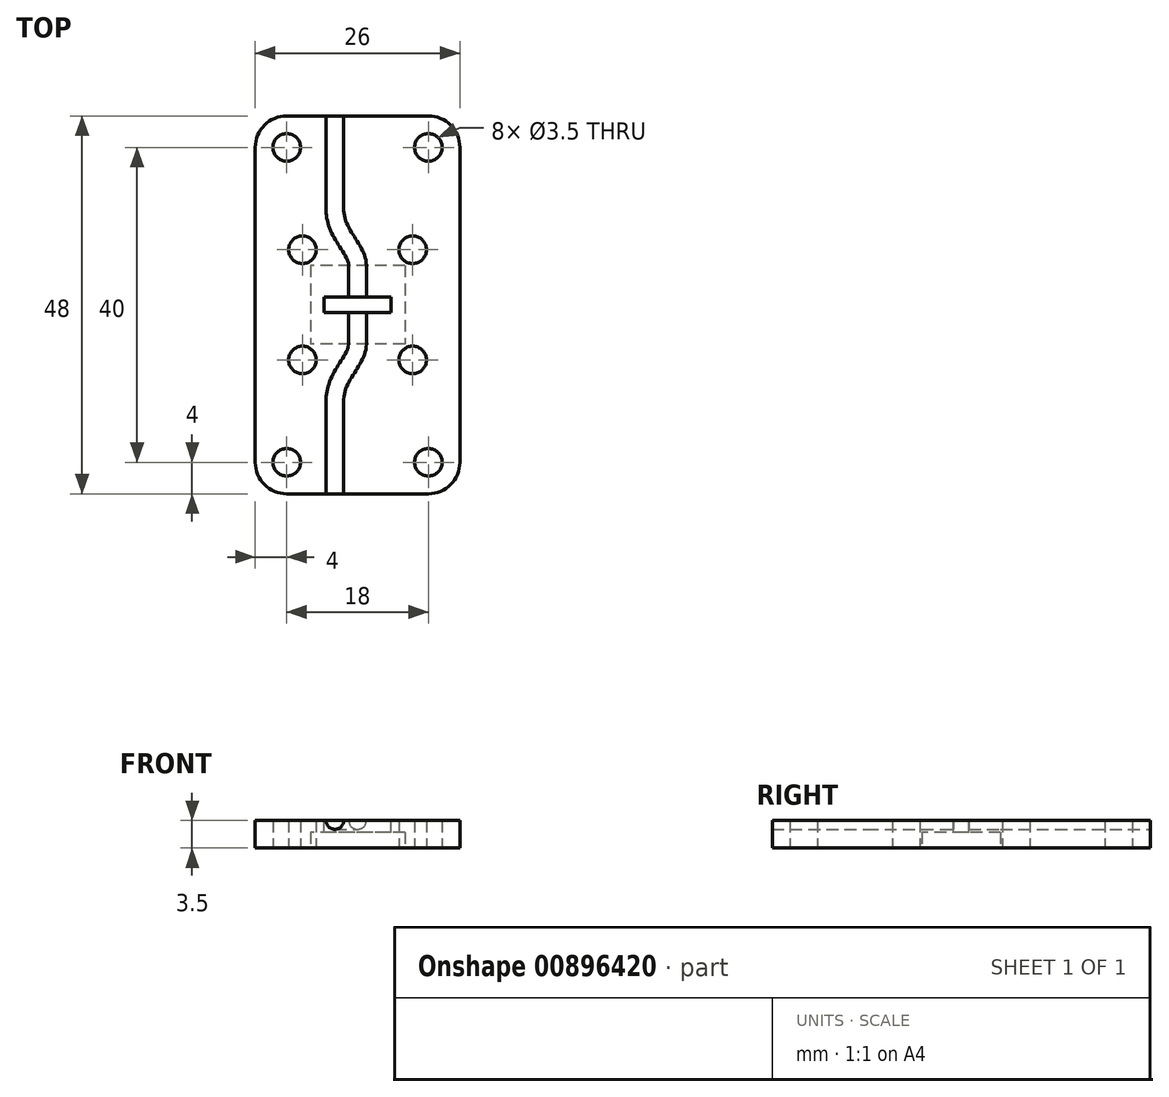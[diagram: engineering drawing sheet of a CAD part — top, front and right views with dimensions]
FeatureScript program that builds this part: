
annotation { "Feature Type Name" : "Feature", "Feature Type Description" : "" }
export const myFeature = defineFeature(function(context is Context, id is Id, definition is map)
    precondition{}
    {
        {
            var Q0;
            Q0=qCreatedBy(makeId("Top.planeOp"),FACE);
            var sketch = newSketch(context, id + "F0", { "sketchPlane" : qUnion([Q0])});
            skCircle(sketch, "E0", {"center": v(-7, 7) * mm, "radius": 1.75 * mm});
            skCircle(sketch, "E1", {"center": v(7, 7) * mm, "radius": 1.75 * mm});
            skCircle(sketch, "E2", {"center": v(7, -7) * mm, "radius": 1.75 * mm});
            skCircle(sketch, "E3", {"center": v(-7, -7) * mm, "radius": 1.75 * mm});
            skCircle(sketch, "E4", {"center": v(9, 20) * mm, "radius": 1.75 * mm});
            skCircle(sketch, "E5", {"center": v(-9, 20) * mm, "radius": 1.75 * mm});
            skCircle(sketch, "E6", {"center": v(-9, -20) * mm, "radius": 1.75 * mm});
            skCircle(sketch, "E7", {"center": v(9, -20) * mm, "radius": 1.75 * mm});
            skArc(sketch, "E8", {"start": v(-9, -24) * mm, "mid": v(-11.83, -22.83) * mm, "end": v(-13, -20) * mm});
            skArc(sketch, "E9", {"start": v(-13, 20) * mm, "mid": v(-11.83, 22.83) * mm, "end": v(-9, 24) * mm});
            skArc(sketch, "E10", {"start": v(9, 24) * mm, "mid": v(11.83, 22.83) * mm, "end": v(13, 20) * mm});
            skArc(sketch, "E11", {"start": v(13, -20) * mm, "mid": v(11.83, -22.83) * mm, "end": v(9, -24) * mm});
            skLineSegment(sketch, "E12", {"start": v(-13, -20) * mm, "end": v(-13, 20) * mm});
            skLineSegment(sketch, "E13", {"start": v(-9, 24) * mm, "end": v(9, 24) * mm});
            skLineSegment(sketch, "E14", {"start": v(13, 20) * mm, "end": v(13, -20) * mm});
            skLineSegment(sketch, "E15", {"start": v(9, -24) * mm, "end": v(-9, -24) * mm});
            skLineSegment(sketch, "E16.bottom", {"start": v(6, 5) * mm, "end": v(-6, 5) * mm});
            skLineSegment(sketch, "E16.top", {"start": v(6, -5) * mm, "end": v(-6, -5) * mm});
            skLineSegment(sketch, "E16.left", {"start": v(6, 5) * mm, "end": v(6, -5) * mm});
            skLineSegment(sketch, "E16.right", {"start": v(-6, 5) * mm, "end": v(-6, -5) * mm});
            skPoint(sketch, "E16.middle", {"position": v(0, 0) * mm});
            skSolve(sketch);
        }
        {
            var Q0;
            Q0=qSketchRegion(id+"F0",true);
            extrude(context, id + "F1", {"entities" : qUnion([Q0]), "depth" : 2 * mm, "offsetDistance" : 25 * mm});
        }
        {
            var Q0;
            Q0=makeQuery(id+"F1.opExtrude","CAP_FACE",FACE,{"disambiguationData":[OSD([sQuery(id+"F0.wireOp",EDGE,"E0"),sQuery(id+"F0.wireOp",EDGE,"E1"),sQuery(id+"F0.wireOp",EDGE,"E2"),sQuery(id+"F0.wireOp",EDGE,"E3"),sQuery(id+"F0.wireOp",EDGE,"E4"),sQuery(id+"F0.wireOp",EDGE,"E5"),sQuery(id+"F0.wireOp",EDGE,"E6"),sQuery(id+"F0.wireOp",EDGE,"E7"),sQuery(id+"F0.wireOp",EDGE,"E8"),sQuery(id+"F0.wireOp",EDGE,"E9"),sQuery(id+"F0.wireOp",EDGE,"E10"),sQuery(id+"F0.wireOp",EDGE,"E11"),sQuery(id+"F0.wireOp",EDGE,"E12"),sQuery(id+"F0.wireOp",EDGE,"E13"),sQuery(id+"F0.wireOp",EDGE,"E14"),sQuery(id+"F0.wireOp",EDGE,"E15"),sQuery(id+"F0.wireOp",EDGE,"E16.bottom"),sQuery(id+"F0.wireOp",EDGE,"E16.top"),sQuery(id+"F0.wireOp",EDGE,"E16.left"),sQuery(id+"F0.wireOp",EDGE,"E16.right")])],"isStart":false});
            var sketch = newSketch(context, id + "F2", { "sketchPlane" : qUnion([Q0])});
            skCircle(sketch, "E17", {"center": v(-7, 7) * mm, "radius": 1.75 * mm});
            skCircle(sketch, "E18", {"center": v(7, -7) * mm, "radius": 1.75 * mm});
            skCircle(sketch, "E19", {"center": v(-7, -7) * mm, "radius": 1.75 * mm});
            skCircle(sketch, "E20", {"center": v(-9, -20) * mm, "radius": 1.75 * mm});
            skCircle(sketch, "E21", {"center": v(-9, 20) * mm, "radius": 1.75 * mm});
            skCircle(sketch, "E22", {"center": v(9, 20) * mm, "radius": 1.75 * mm});
            skCircle(sketch, "E23", {"center": v(9, -20) * mm, "radius": 1.75 * mm});
            skCircle(sketch, "E24", {"center": v(7, 7) * mm, "radius": 1.75 * mm});
            skArc(sketch, "E25", {"start": v(-9, -24) * mm, "mid": v(-11.83, -22.83) * mm, "end": v(-13, -20) * mm});
            skArc(sketch, "E26", {"start": v(-13, 20) * mm, "mid": v(-11.83, 22.83) * mm, "end": v(-9, 24) * mm});
            skArc(sketch, "E27", {"start": v(9, 24) * mm, "mid": v(11.83, 22.83) * mm, "end": v(13, 20) * mm});
            skArc(sketch, "E28", {"start": v(13, -20) * mm, "mid": v(11.83, -22.83) * mm, "end": v(9, -24) * mm});
            skLineSegment(sketch, "E29", {"start": v(-13, -20) * mm, "end": v(-13, 20) * mm});
            skLineSegment(sketch, "E30", {"start": v(-9, 24) * mm, "end": v(9, 24) * mm});
            skLineSegment(sketch, "E31", {"start": v(13, 20) * mm, "end": v(13, -20) * mm});
            skLineSegment(sketch, "E32", {"start": v(9, -24) * mm, "end": v(-9, -24) * mm});
            skSolve(sketch);
        }
        {
            var Q0;
            Q0=qSketchRegion(id+"F2",true);
            extrude(context, id + "F3", {"entities" : qUnion([Q0]), "operationType" : NewBodyOperationType.ADD, "depth" : 1.5 * mm, "offsetDistance" : 25 * mm});
        }
        {
            var Q0;
            Q0=makeQuery(id+"F3.opExtrude","CAP_FACE",FACE,{"disambiguationData":[OSD([sQuery(id+"F2.wireOp",EDGE,"E17"),sQuery(id+"F2.wireOp",EDGE,"E18"),sQuery(id+"F2.wireOp",EDGE,"E19"),sQuery(id+"F2.wireOp",EDGE,"E20"),sQuery(id+"F2.wireOp",EDGE,"E21"),sQuery(id+"F2.wireOp",EDGE,"E22"),sQuery(id+"F2.wireOp",EDGE,"E23"),sQuery(id+"F2.wireOp",EDGE,"E24"),sQuery(id+"F2.wireOp",EDGE,"E25"),sQuery(id+"F2.wireOp",EDGE,"E26"),sQuery(id+"F2.wireOp",EDGE,"E27"),sQuery(id+"F2.wireOp",EDGE,"E28"),sQuery(id+"F2.wireOp",EDGE,"E29"),sQuery(id+"F2.wireOp",EDGE,"E30"),sQuery(id+"F2.wireOp",EDGE,"E31"),sQuery(id+"F2.wireOp",EDGE,"E32")])],"isStart":false});
            var sketch = newSketch(context, id + "F4", { "sketchPlane" : qUnion([Q0])});
            skLineSegment(sketch, "E33.bottom", {"start": v(4.25, 1) * mm, "end": v(-4.25, 1) * mm});
            skLineSegment(sketch, "E33.top", {"start": v(4.25, -1) * mm, "end": v(-4.25, -1) * mm});
            skLineSegment(sketch, "E33.left", {"start": v(4.25, 1) * mm, "end": v(4.25, -1) * mm});
            skLineSegment(sketch, "E33.right", {"start": v(-4.25, 1) * mm, "end": v(-4.25, -1) * mm});
            skPoint(sketch, "E33.middle", {"position": v(0, 0) * mm});
            skSolve(sketch);
        }
        {
            var Q0;
            Q0=qSketchRegion(id+"F4",true);
            extrude(context, id + "F5", {"entities" : qUnion([Q0]), "depth" : -5 * mm, "offsetDistance" : 25 * mm});
        }
        {
            var Q0;
            Q0=makeQuery(id+"Ft503yfXoWAvfJn_1.opExtrude","SWEPT_BODY",BODY,{"disambiguationData":[OSD([sQuery(id+"FCbR6J0HlV25bnM_1.wireOp",EDGE,"kRnqYj1O-LiRQ-OpM5-NT83-xEiEe5cHpb25")])]});
            var Q1;
            Q1=makeQuery(id+"F5.opExtrude","SWEPT_BODY",BODY,{"disambiguationData":[OSD([sQuery(id+"F4.wireOp",EDGE,"E33.bottom"),sQuery(id+"F4.wireOp",EDGE,"E33.top"),sQuery(id+"F4.wireOp",EDGE,"E33.left"),sQuery(id+"F4.wireOp",EDGE,"E33.right")])]});
            var Q2;
            Q2=makeQuery(id+"F1.opExtrude","SWEPT_BODY",BODY,{"disambiguationData":[OSD([sQuery(id+"F0.wireOp",EDGE,"E0"),sQuery(id+"F0.wireOp",EDGE,"E1"),sQuery(id+"F0.wireOp",EDGE,"E2"),sQuery(id+"F0.wireOp",EDGE,"E3"),sQuery(id+"F0.wireOp",EDGE,"E4"),sQuery(id+"F0.wireOp",EDGE,"E5"),sQuery(id+"F0.wireOp",EDGE,"E6"),sQuery(id+"F0.wireOp",EDGE,"E7"),sQuery(id+"F0.wireOp",EDGE,"E8"),sQuery(id+"F0.wireOp",EDGE,"E9"),sQuery(id+"F0.wireOp",EDGE,"E10"),sQuery(id+"F0.wireOp",EDGE,"E11"),sQuery(id+"F0.wireOp",EDGE,"E12"),sQuery(id+"F0.wireOp",EDGE,"E13"),sQuery(id+"F0.wireOp",EDGE,"E14"),sQuery(id+"F0.wireOp",EDGE,"E15"),sQuery(id+"F0.wireOp",EDGE,"E16.bottom"),sQuery(id+"F0.wireOp",EDGE,"E16.top"),sQuery(id+"F0.wireOp",EDGE,"E16.left"),sQuery(id+"F0.wireOp",EDGE,"E16.right")])]});
            booleanBodies(context, id + "F6", {"operationType" : BooleanOperationType.SUBTRACTION, "tools" : qUnion([Q0, Q1]), "targets" : qUnion([Q2])});
        }
        {
            var Q0;
            Q0=makeQuery(id+"F3.opExtrude","CAP_FACE",FACE,{"disambiguationData":[OSD([sQuery(id+"F2.wireOp",EDGE,"E17"),sQuery(id+"F2.wireOp",EDGE,"E18"),sQuery(id+"F2.wireOp",EDGE,"E19"),sQuery(id+"F2.wireOp",EDGE,"E20"),sQuery(id+"F2.wireOp",EDGE,"E21"),sQuery(id+"F2.wireOp",EDGE,"E22"),sQuery(id+"F2.wireOp",EDGE,"E23"),sQuery(id+"F2.wireOp",EDGE,"E24"),sQuery(id+"F2.wireOp",EDGE,"E25"),sQuery(id+"F2.wireOp",EDGE,"E26"),sQuery(id+"F2.wireOp",EDGE,"E27"),sQuery(id+"F2.wireOp",EDGE,"E28"),sQuery(id+"F2.wireOp",EDGE,"E29"),sQuery(id+"F2.wireOp",EDGE,"E30"),sQuery(id+"F2.wireOp",EDGE,"E31"),sQuery(id+"F2.wireOp",EDGE,"E32")])],"isStart":false});
            var sketch = newSketch(context, id + "F7", { "sketchPlane" : qUnion([Q0])});
            skLineSegment(sketch, "E34.bottom", {"start": v(-4, -24) * mm, "end": v(-1.75, -24) * mm});
            skLineSegment(sketch, "E34.top", {"start": v(-4, -12) * mm, "end": v(-1.75, -12) * mm});
            skLineSegment(sketch, "E34.left", {"start": v(-4, -24) * mm, "end": v(-4, -12) * mm});
            skLineSegment(sketch, "E34.right", {"start": v(-1.75, -24) * mm, "end": v(-1.75, -12) * mm});
            skLineSegment(sketch, "E35.bottom", {"start": v(-4, 24) * mm, "end": v(-1.75, 24) * mm});
            skLineSegment(sketch, "E35.top", {"start": v(-4, 12) * mm, "end": v(-1.75, 12) * mm});
            skLineSegment(sketch, "E35.left", {"start": v(-4, 24) * mm, "end": v(-4, 12) * mm});
            skLineSegment(sketch, "E35.right", {"start": v(-1.75, 24) * mm, "end": v(-1.75, 12) * mm});
            skLineSegment(sketch, "E36.bottom", {"start": v(1.12, 5) * mm, "end": v(-1.13, 5) * mm});
            skLineSegment(sketch, "E36.top", {"start": v(1.12, -5) * mm, "end": v(-1.13, -5) * mm});
            skLineSegment(sketch, "E36.left", {"start": v(1.12, 5) * mm, "end": v(1.12, -5) * mm});
            skLineSegment(sketch, "E36.right", {"start": v(-1.13, 5) * mm, "end": v(-1.13, -5) * mm});
            skPoint(sketch, "E36.middle", {"position": v(0, 0) * mm});
            skFitSpline(sketch, "E37", {"points": [v(-4, 12) * mm, v(-1.13, 5) * mm], "startDerivative": vector(0, -7.36) * mm, "endDerivative": vector(0, -7.36) * mm});
            skFitSpline(sketch, "E38", {"points": [v(-1.75, 12) * mm, v(1.12, 5) * mm], "startDerivative": vector(0, -7.36) * mm, "endDerivative": vector(0, -7.36) * mm});
            skFitSpline(sketch, "E39", {"points": [v(-4, -12) * mm, v(-1.13, -5) * mm], "startDerivative": vector(0, 7.23) * mm, "endDerivative": vector(0, 7.23) * mm});
            skFitSpline(sketch, "E40", {"points": [v(-1.75, -12) * mm, v(1.12, -5) * mm], "startDerivative": vector(0, 7.23) * mm, "endDerivative": vector(0, 7.23) * mm});
            skSolve(sketch);
        }
        {
            var Q0;
            Q0=makeQuery(id+"F3.boolean.opBoolean","MERGE",FACE,{"derivedFrom":[makeQuery(id+"F1.opExtrude","SWEPT_FACE",FACE,{"disambiguationData":[OSD([sQuery(id+"F0.wireOp",EDGE,"E15")])]}),makeQuery(id+"F3.opExtrude","SWEPT_FACE",FACE,{"disambiguationData":[OSD([sQuery(id+"F2.wireOp",EDGE,"E32")])]})]});
            var sketch = newSketch(context, id + "F8", { "sketchPlane" : qUnion([Q0])});
            skCircle(sketch, "E41", {"center": v(-2.87, 3.5) * mm, "radius": 1.13 * mm});
            skSolve(sketch);
        }
        {
            var Q0;
            {var subQ0=sQuery(id+"F8.wireOp",EDGE,"E41");var subQ1=makeQuery(id+"F3.opExtrude","CAP_EDGE",EDGE,{"disambiguationData":[OSD([sQuery(id+"F2.wireOp",EDGE,"E32")])],"isStart":false});var subQ2=makeQuery(id+"F8.imprint","INTERSECT",VERTEX,{"disambiguationData":[OD(0.0)],"derivedFrom":[subQ1,subQ0]});Q0=makeQuery(id+"F8.imprint","IMPRINT",FACE,{"disambiguationData":[TD([[makeQuery(id+"F8.imprint","IMPRINT",EDGE,{"disambiguationData":[TD([[subQ2,1.0]])],"derivedFrom":subQ0}),1.0]])]});}
            var Q1;
            {var subQ0=sQuery(id+"F8.wireOp",EDGE,"E41");var subQ1=makeQuery(id+"F3.opExtrude","CAP_EDGE",EDGE,{"disambiguationData":[OSD([sQuery(id+"F2.wireOp",EDGE,"E32")])],"isStart":false});var subQ2=makeQuery(id+"F8.imprint","INTERSECT",VERTEX,{"disambiguationData":[OD(0.0)],"derivedFrom":[subQ1,subQ0]});Q1=makeQuery(id+"F8.imprint","IMPRINT",FACE,{"disambiguationData":[TD([[makeQuery(id+"F8.imprint","IMPRINT",EDGE,{"disambiguationData":[TD([[subQ2,-1.0]])],"derivedFrom":subQ0}),1.0]])]});}
            var Q2;
            Q2=sQuery(id+"F7.wireOp",EDGE,"E34.right");
            var Q3;
            Q3=sQuery(id+"F7.wireOp",EDGE,"E40");
            var Q4;
            Q4=sQuery(id+"F7.wireOp",EDGE,"E36.left");
            var Q5;
            Q5=sQuery(id+"F7.wireOp",EDGE,"E38");
            var Q6;
            Q6=sQuery(id+"F7.wireOp",EDGE,"E35.right");
            sweep(context, id + "F9", {"profiles" : qUnion([Q0, Q1]), "path" : qUnion([Q2, Q3, Q4, Q5, Q6])});
        }
        {
            var Q0;
            Q0=makeQuery(id+"F9.opSweep","SWEPT_BODY",BODY,{"disambiguationData":[OSD([sQuery(id+"F7.wireOp",EDGE,"E35.right"),sQuery(id+"F8.wireOp",EDGE,"E41")])]});
            var Q1;
            Q1=makeQuery(id+"F1.opExtrude","SWEPT_BODY",BODY,{"disambiguationData":[OSD([sQuery(id+"F0.wireOp",EDGE,"E0"),sQuery(id+"F0.wireOp",EDGE,"E1"),sQuery(id+"F0.wireOp",EDGE,"E2"),sQuery(id+"F0.wireOp",EDGE,"E3"),sQuery(id+"F0.wireOp",EDGE,"E4"),sQuery(id+"F0.wireOp",EDGE,"E5"),sQuery(id+"F0.wireOp",EDGE,"E6"),sQuery(id+"F0.wireOp",EDGE,"E7"),sQuery(id+"F0.wireOp",EDGE,"E8"),sQuery(id+"F0.wireOp",EDGE,"E9"),sQuery(id+"F0.wireOp",EDGE,"E10"),sQuery(id+"F0.wireOp",EDGE,"E11"),sQuery(id+"F0.wireOp",EDGE,"E12"),sQuery(id+"F0.wireOp",EDGE,"E13"),sQuery(id+"F0.wireOp",EDGE,"E14"),sQuery(id+"F0.wireOp",EDGE,"E15"),sQuery(id+"F0.wireOp",EDGE,"E16.bottom"),sQuery(id+"F0.wireOp",EDGE,"E16.top"),sQuery(id+"F0.wireOp",EDGE,"E16.left"),sQuery(id+"F0.wireOp",EDGE,"E16.right")])]});
            booleanBodies(context, id + "F10", {"operationType" : BooleanOperationType.SUBTRACTION, "tools" : qUnion([Q0]), "targets" : qUnion([Q1])});
        }
    });
